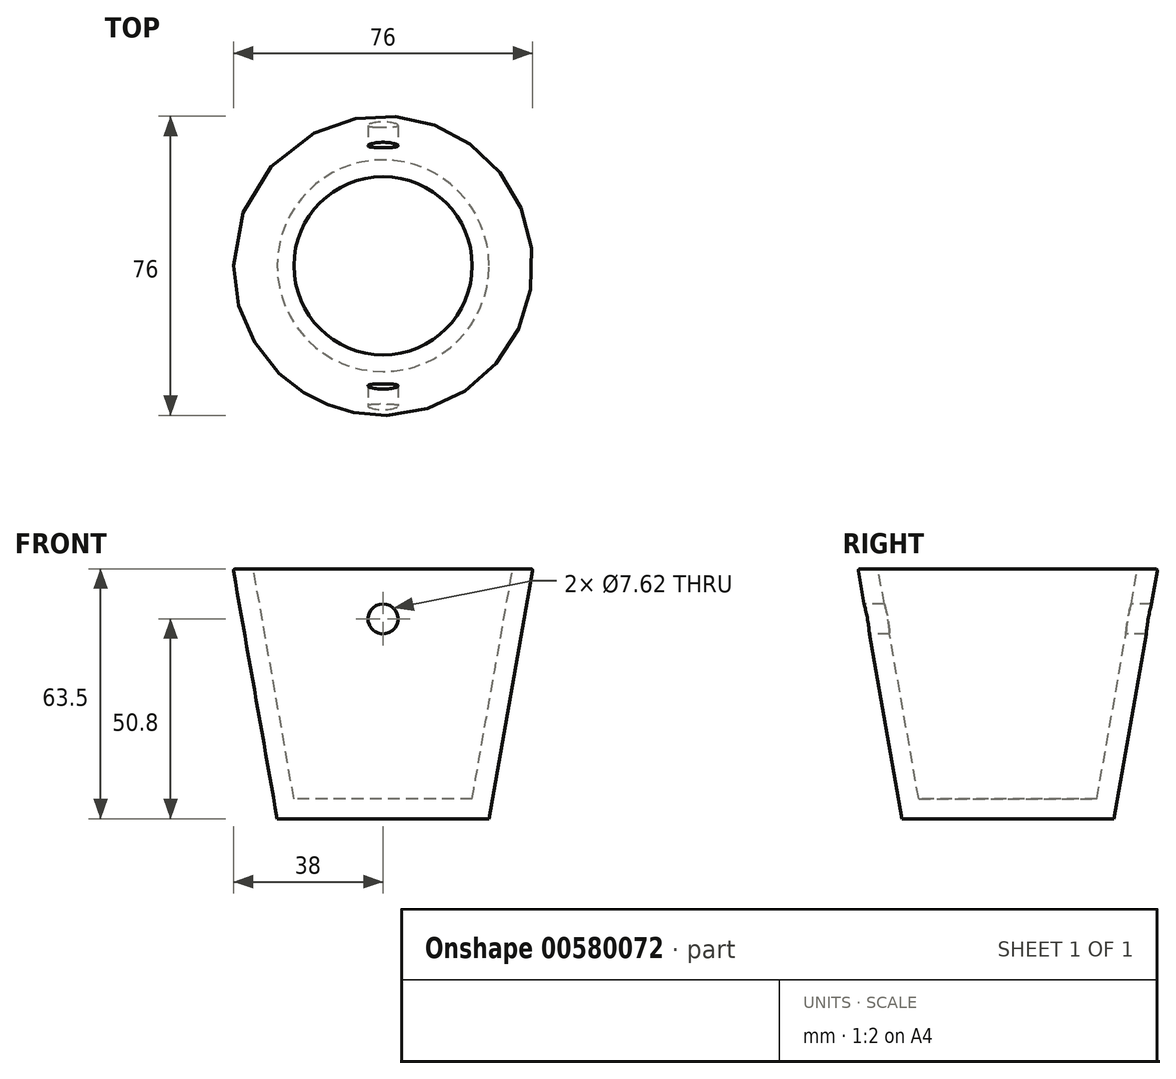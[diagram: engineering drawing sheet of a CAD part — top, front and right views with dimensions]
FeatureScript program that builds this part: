
annotation { "Feature Type Name" : "Feature", "Feature Type Description" : "" }
export const myFeature = defineFeature(function(context is Context, id is Id, definition is map)
    precondition{}
    {
        {
            var Q0;
            Q0=qCreatedBy(makeId("Front.planeOp"),FACE);
            var sketch = newSketch(context, id + "F0", { "sketchPlane" : qUnion([Q0])});
            skLineSegment(sketch, "E0", {"start": v(0, 63.5) * mm, "end": v(-38.1, 63.5) * mm});
            skLineSegment(sketch, "E1", {"start": v(-38.1, 63.5) * mm, "end": v(-26.9, 0) * mm});
            skLineSegment(sketch, "E2", {"start": v(-26.9, 0) * mm, "end": v(0, 0) * mm});
            skLineSegment(sketch, "E3", {"start": v(0, 0) * mm, "end": v(0, 63.5) * mm});
            skSolve(sketch);
        }
        {
            var Q0;
            Q0=makeQuery(id+"F0.imprint","IMPRINT",FACE,{"disambiguationData":[TD([[makeQuery(id+"F0.imprint","IMPRINT",EDGE,{"derivedFrom":sQuery(id+"F0.wireOp",EDGE,"E0")}),1.0]])]});
            var Q1;
            Q1=sQuery(id+"F0.wireOp",EDGE,"E3");
            revolve(context, id + "F1", {"entities" : qUnion([Q0]), "axis" : qUnion([Q1]), "revolveType" : RevolveType.FULL});
        }
        {
            var Q0;
            Q0=makeQuery(id+"F1.opRevolve","SWEPT_FACE",FACE,{"disambiguationData":[OSD([sQuery(id+"F0.wireOp",EDGE,"E0")])]});
            shell(context, id + "F2", {"entities" : qUnion([Q0]), "thickness" : 5.08 * mm});
        }
        {
            var Q0;
            Q0=qCreatedBy(makeId("Front.planeOp"),FACE);
            var sketch = newSketch(context, id + "F3", { "sketchPlane" : qUnion([Q0])});
            skCircle(sketch, "E4", {"center": v(0, 50.8) * mm, "radius": 3.81 * mm});
            skSolve(sketch);
        }
        {
            var Q0;
            Q0=makeQuery(id+"F3.imprint","IMPRINT",FACE,{"disambiguationData":[TD([[makeQuery(id+"F3.imprint","IMPRINT",EDGE,{"derivedFrom":sQuery(id+"F3.wireOp",EDGE,"E4")}),1.0]])]});
            extrude(context, id + "F4", {"entities" : qUnion([Q0]), "operationType" : NewBodyOperationType.REMOVE, "oppositeDirection" : true, "depth" : 103.63 * mm, "offsetDistance" : 25.4 * mm, "symmetric" : true});
        }
        {
            var Q0;
            Q0=makeQuery(id+"F1.opRevolve","SWEPT_FACE",FACE,{"disambiguationData":[OSD([sQuery(id+"F0.wireOp",EDGE,"E0")])]});
            fillet(context, id + "F5", {"entities" : qUnion([Q0]), "radius" : 0.5 * mm, "tangentPropagation" : true, "allowEdgeOverflow" : false});
        }
    });
